# Revit family: NLRS_57_AIR_UN_airflow-arrow-open-end-rectangular-duct-in_sacs
name_source: partatom
category: Air Terminals
units: mm (PartAtom-declared; Revit-internal decimal feet)

## family parameters
Always vertical = Yes
Cut with Voids When Loaded = No
Part Type = Normal
Room Calculation Point = No
Round Connector Dimension = Use Diameter
Shared = No
Work Plane-Based = No

## types (3) — shared parameters
Assembly Code = 57.00
Description = Rectangular open end, airflow duct IN
IfcDescription = Rectangular open end, airflow duct IN
IfcExportAs = IfcAirTerminal
IfcExportType = OPEN END
Manufacturer = Solid Air Climate Systems
Model = Airflow arrow - duct IN
NLRS_C_content_datum_uitgifte = 09-06-2023
NLRS_C_content_provider = Solid Air Climate Systems
NLRS_C_content_versie = 1.20.00
NLRS_C_description = Rectangular open end, airflow duct IN
NLRS_C_model = Airflow arrow - duct IN
URL = https://solid-air.nl
zero-valued in all types: Default Elevation

## per-type parameters (varying)
| type | Size_multiplier |
| Size 1 | 1 |
| Size 1.5 | 1.5 |
| Size 2 | 2 |

## geometry (parser evidence)
native form markers: Sweep x6
no freeform markers — native parametric forms only
